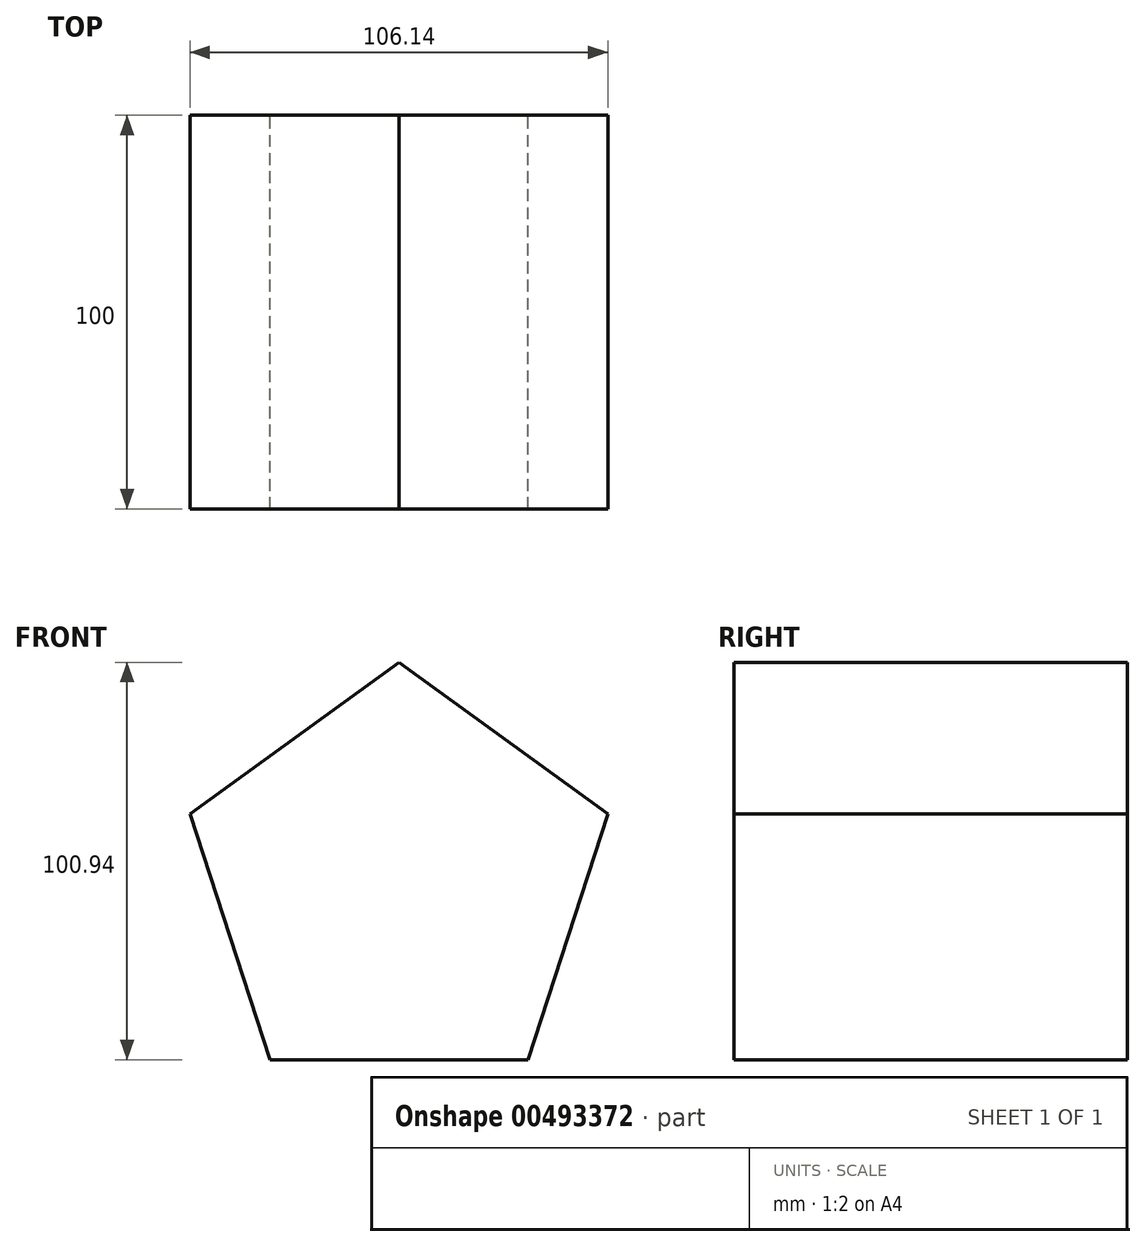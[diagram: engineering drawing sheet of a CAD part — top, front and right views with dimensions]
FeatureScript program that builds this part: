
annotation { "Feature Type Name" : "Feature", "Feature Type Description" : "" }
export const myFeature = defineFeature(function(context is Context, id is Id, definition is map)
    precondition{}
    {
        {
            var Q0;
            Q0=qCreatedBy(makeId("Front.planeOp"),FACE);
            var sketch = newSketch(context, id + "F0", { "sketchPlane" : qUnion([Q0])});
            skCircle(sketch, "E0.cCircle", {"center": v(0, 0) * mm, "radius": 55.8 * mm, "construction": true});
            skLineSegment(sketch, "E0.0", {"start": v(0, 55.8) * mm, "end": v(53.07, 17.24) * mm});
            skLineSegment(sketch, "E0.1", {"start": v(53.07, 17.24) * mm, "end": v(32.8, -45.14) * mm});
            skLineSegment(sketch, "E0.2", {"start": v(32.8, -45.14) * mm, "end": v(-32.8, -45.14) * mm});
            skLineSegment(sketch, "E0.3", {"start": v(-32.8, -45.14) * mm, "end": v(-53.07, 17.24) * mm});
            skLineSegment(sketch, "E0.4", {"start": v(-53.07, 17.24) * mm, "end": v(0, 55.8) * mm});
            skSolve(sketch);
        }
        {
            var Q0;
            Q0=makeQuery(id+"F0.imprint","IMPRINT",FACE,{"disambiguationData":[TD([[makeQuery(id+"F0.imprint","IMPRINT",EDGE,{"derivedFrom":sQuery(id+"F0.wireOp",EDGE,"E0.0")}),-1.0]])]});
            extrude(context, id + "F1", {"entities" : qUnion([Q0]), "endBound" : BoundingType.SYMMETRIC, "depth" : 100 * mm});
        }
    });
